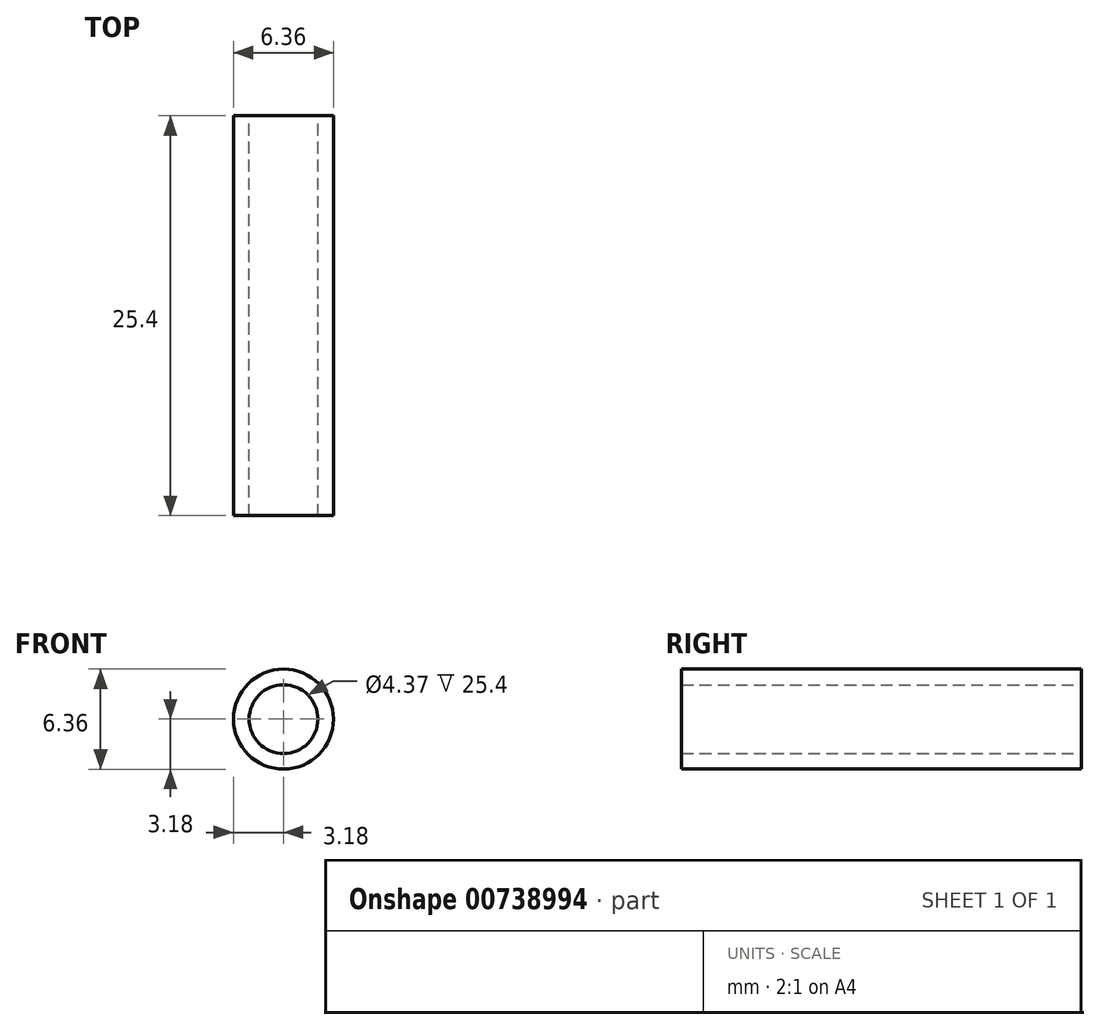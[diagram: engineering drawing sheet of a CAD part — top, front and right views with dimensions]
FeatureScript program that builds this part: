
annotation { "Feature Type Name" : "Feature", "Feature Type Description" : "" }
export const myFeature = defineFeature(function(context is Context, id is Id, definition is map)
    precondition{}
    {
        {
            var Q0;
            Q0=qCreatedBy(makeId("Front.planeOp"),FACE);
            var sketch = newSketch(context, id + "F0", { "sketchPlane" : qUnion([Q0])});
            skCircle(sketch, "E0", {"center": v(0, 0) * mm, "radius": 2.18 * mm});
            skCircle(sketch, "E1", {"center": v(0, 0) * mm, "radius": 3.18 * mm});
            skSolve(sketch);
        }
        {
            var Q0;
            Q0 = qSketchRegion(id + "F0", true);
            extrude(context, id + "F1", {"entities" : qUnion([Q0]), "depth" : 25.4 * mm, "offsetDistance" : 25.4 * mm});
        }
    });
